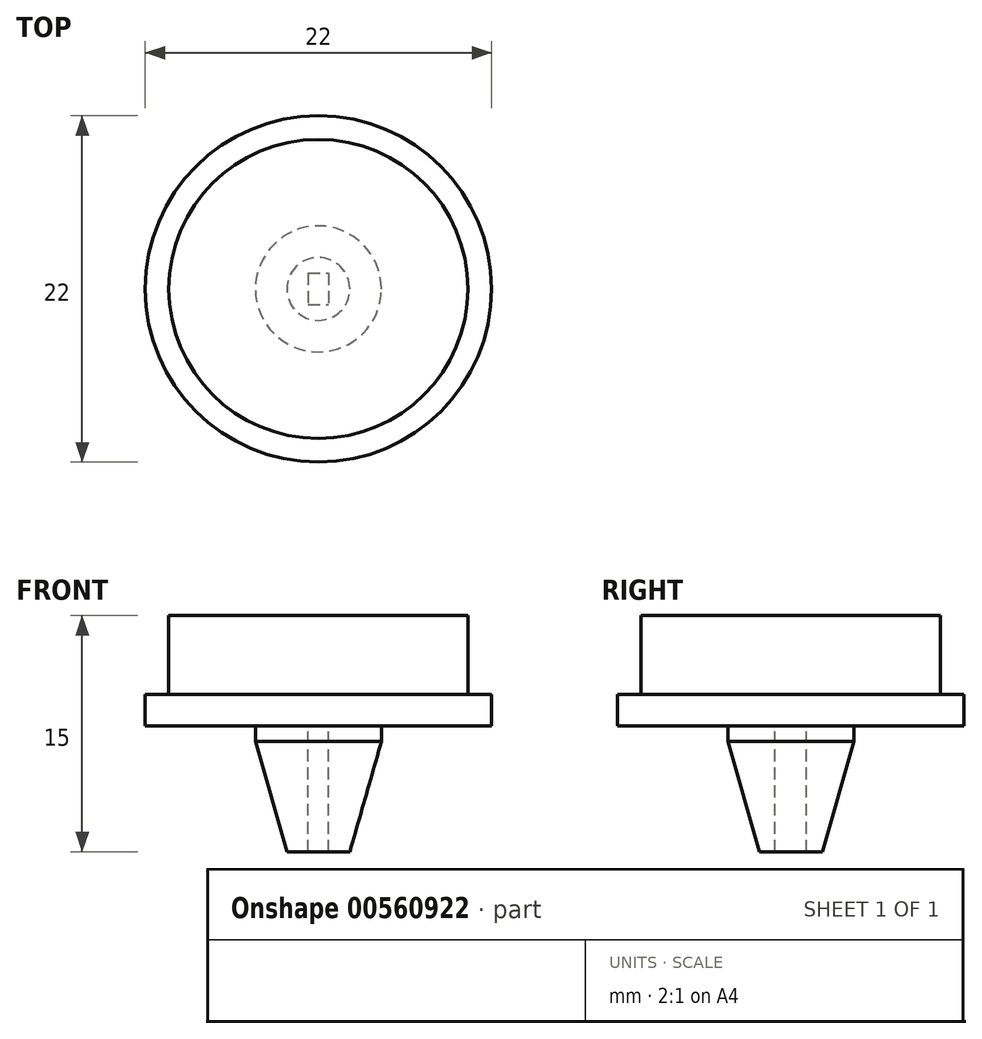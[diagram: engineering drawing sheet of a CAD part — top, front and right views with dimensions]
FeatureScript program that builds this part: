
annotation { "Feature Type Name" : "Feature", "Feature Type Description" : "" }
export const myFeature = defineFeature(function(context is Context, id is Id, definition is map)
    precondition{}
    {
        {
            var Q0;
            Q0=qCreatedBy(makeId("Top.planeOp"),FACE);
            var sketch = newSketch(context, id + "F0", { "sketchPlane" : qUnion([Q0])});
            skCircle(sketch, "E0", {"center": v(0, 0) * mm, "radius": 9.5 * mm});
            skCircle(sketch, "E1", {"center": v(0, 0) * mm, "radius": 11 * mm});
            skLineSegment(sketch, "E2.bottom", {"start": v(-0.65, 1) * mm, "end": v(0.65, 1) * mm});
            skLineSegment(sketch, "E2.top", {"start": v(-0.65, -1) * mm, "end": v(0.65, -1) * mm});
            skLineSegment(sketch, "E2.left", {"start": v(-0.65, 1) * mm, "end": v(-0.65, -1) * mm});
            skLineSegment(sketch, "E2.right", {"start": v(0.65, 1) * mm, "end": v(0.65, -1) * mm});
            skCircle(sketch, "E3", {"center": v(0, 0) * mm, "radius": 4 * mm});
            skSolve(sketch);
        }
        {
            var Q0;
            Q0=makeQuery(id+"F0.imprint","IMPRINT",FACE,{"disambiguationData":[TD([[makeQuery(id+"F0.imprint","IMPRINT",EDGE,{"derivedFrom":sQuery(id+"F0.wireOp",EDGE,"E0")}),-1.0]])]});
            var Q1;
            Q1=makeQuery(id+"F0.imprint","IMPRINT",FACE,{"disambiguationData":[TD([[makeQuery(id+"F0.imprint","IMPRINT",EDGE,{"derivedFrom":sQuery(id+"F0.wireOp",EDGE,"E0")}),1.0]])]});
            var Q2;
            Q2=makeQuery(id+"F0.imprint","IMPRINT",FACE,{"disambiguationData":[TD([[makeQuery(id+"F0.imprint","IMPRINT",EDGE,{"derivedFrom":sQuery(id+"F0.wireOp",EDGE,"E2.bottom")}),1.0]])]});
            var Q3;
            Q3=makeQuery(id+"F0.imprint","IMPRINT",FACE,{"disambiguationData":[TD([[makeQuery(id+"F0.imprint","IMPRINT",EDGE,{"derivedFrom":sQuery(id+"F0.wireOp",EDGE,"E2.bottom")}),-1.0]])]});
            extrude(context, id + "F1", {"entities" : qUnion([Q0, Q1, Q2, Q3]), "oppositeDirection" : true, "depth" : 2 * mm, "offsetDistance" : 25 * mm});
        }
        {
            var Q0;
            Q0=makeQuery(id+"F0.imprint","IMPRINT",FACE,{"disambiguationData":[TD([[makeQuery(id+"F0.imprint","IMPRINT",EDGE,{"derivedFrom":sQuery(id+"F0.wireOp",EDGE,"E0")}),1.0]])]});
            var Q1;
            Q1=makeQuery(id+"F0.imprint","IMPRINT",FACE,{"disambiguationData":[TD([[makeQuery(id+"F0.imprint","IMPRINT",EDGE,{"derivedFrom":sQuery(id+"F0.wireOp",EDGE,"E2.bottom")}),1.0]])]});
            var Q2;
            Q2=makeQuery(id+"F0.imprint","IMPRINT",FACE,{"disambiguationData":[TD([[makeQuery(id+"F0.imprint","IMPRINT",EDGE,{"derivedFrom":sQuery(id+"F0.wireOp",EDGE,"E2.bottom")}),-1.0]])]});
            extrude(context, id + "F2", {"entities" : qUnion([Q0, Q1, Q2]), "operationType" : NewBodyOperationType.ADD, "depth" : 5 * mm, "offsetDistance" : 25 * mm});
        }
        {
            var Q0;
            Q0=makeQuery(id+"F0.imprint","IMPRINT",FACE,{"disambiguationData":[TD([[makeQuery(id+"F0.imprint","IMPRINT",EDGE,{"derivedFrom":sQuery(id+"F0.wireOp",EDGE,"E2.bottom")}),1.0]])]});
            extrude(context, id + "F3", {"entities" : qUnion([Q0]), "operationType" : NewBodyOperationType.ADD, "oppositeDirection" : true, "depth" : 10 * mm, "offsetDistance" : 25 * mm});
        }
        {
            var Q0;
            Q0=makeQuery(id+"F3.opExtrude","CAP_EDGE",EDGE,{"disambiguationData":[OSD([sQuery(id+"F0.wireOp",EDGE,"E3")])],"isStart":false});
            chamfer(context, id + "F4", {"entities" : qUnion([Q0]), "chamferType" : ChamferType.TWO_OFFSETS, "width1" : 7 * mm, "oppositeDirection" : false, "width2" : 2 * mm, "tangentPropagation" : true});
        }
    });
